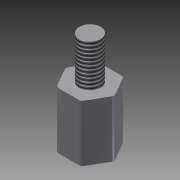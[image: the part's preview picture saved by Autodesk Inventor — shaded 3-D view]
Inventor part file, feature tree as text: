
AUTODESK INVENTOR PART (.ipt)
format: ipt  version: 2013 (Build 170138000, 138)  size: 106,496 bytes
history: native  units: mm
features: sketch x3, extrude x2, thread x2, other x1, hole x1, fillet x1
ambient origin geometry x1: Origin
feature tree (10):
  other  "ソリッド1"
  extrude  "押し出し1"  Depth=6.0mm
  extrude  "押し出し2"  Depth=3.0mm
  hole  "穴1"  [1 undecoded]
  thread  "ねじ1"
  thread  "ねじ2"
  fillet  "フィレット1"  Radius=3.0mm
  sketch  "スケッチ1"
  sketch  "スケッチ2"
  sketch  "スケッチ3"
note: 1 required parameter value undecoded (feature->parameter linkage not recoverable at this tier; creation-order binding heuristic only, values carry confidence <= 0.55)
